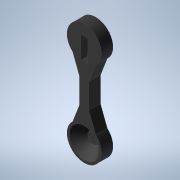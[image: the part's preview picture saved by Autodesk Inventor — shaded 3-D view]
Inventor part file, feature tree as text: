
AUTODESK INVENTOR PART (.ipt)
format: ipt  version: 2022 (Build 260153000, 153)  size: 201,728 bytes
history: native  units: in
note: dims shown in document units (in); Inventor stores cm internally (conversion verified against a paired STEP export)
features: extrude x8, sketch x8, chamfer x1
ambient origin geometry x8: Origin, YZ Plane, XZ Plane, XY Plane, X Axis, Y Axis, Z Axis, Center Point
bodies: Solid1 (feature_tree)
feature tree (17):
  extrude  "Extrusion1"  Depth=0.7874in
  extrude  "Extrusion2"  Depth=0.7874in
  extrude  "Extrusion3"  Depth=0.7874in TaperAngle=0.0deg
  extrude  "Extrusion4"  Depth=0.6299in TaperAngle=0.0deg
  extrude  "Extrusion5"  Depth=0.1181in
  extrude  "Extrusion6"  Depth=0.1181in TaperAngle=0.0deg
  extrude  "Extrusion7"  Depth=0.7874in
  chamfer  "Chamfer1"  Distance=0.9055in
  extrude  "Extrusion8"  Depth=0.5118in TaperAngle=0.0deg
  sketch  "Sketch1"  dims[d0=2.3622in d1=0.7874in]
  sketch  "Sketch2"  dims[d2=5.9055in d3=0.7874in]
  sketch  "Sketch3"  dims[d4=2.3622in d5=0.7874in d6=0.0in]
  sketch  "Sketch4"  dims[d7=0.7874in d8=0.6299in d9=0.0in]
  sketch  "Sketch5"  dims[d10=0.1181in d11=0.1181in]
  sketch  "Sketch6"  dims[d12=0.1181in d13=0.9951in d14=0.0in]
  sketch  "Sketch7"  dims[d15=0.7874in d16=1.5748in]
  sketch  "Sketch8"  dims[d17=0.4724in d18=0.9055in d19=0.5118in d20=0.0in d21=0.185in d22=0.185in d23=0.4528in d24=0.0in d25=0.0906in d26=0.0787in d27=0.0906in d28=0.0787in d29=0.1969in d30=0.0in d31=0.7874in d32=0.315in d33=0.0in d34=0.6299in d35=0.0787in d36=45.0deg d37=2.5251in d38=0.0in]
